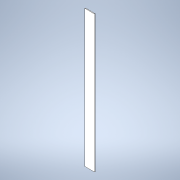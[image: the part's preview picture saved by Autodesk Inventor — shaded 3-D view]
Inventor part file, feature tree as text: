
AUTODESK INVENTOR PART (.ipt)
format: ipt  version: 2022 (Build 260153000, 153)  size: 93,696 bytes
history: native  units: in
note: dims shown in document units (in); Inventor stores cm internally (conversion verified against a paired STEP export)
features: extrude x1, sketch x1
ambient origin geometry x8: Origin, YZ Plane, XZ Plane, XY Plane, X Axis, Y Axis, Z Axis, Center Point
bodies: Solid1 (feature_tree)
feature tree (2):
  extrude  "Extrusion1"  Depth=0.1969in
  sketch  "Sketch1"  dims[d0=2.9528in d1=0.1969in d2=40.5512in d3=0.0in]
